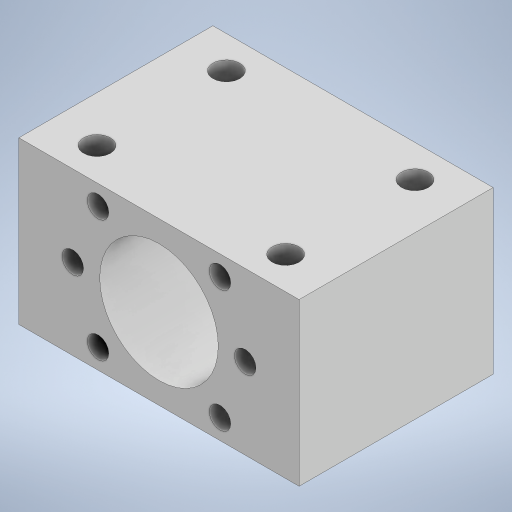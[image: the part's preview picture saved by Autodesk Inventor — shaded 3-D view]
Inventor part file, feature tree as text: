
AUTODESK INVENTOR PART (.ipt)
format: ipt  version: 2023 (Build 270158000, 158)  size: 224,768 bytes
history: native  units: mm
features: extrude x2, sketch x2
ambient origin geometry x8: Origin, YZ Plane, XZ Plane, XY Plane, X Axis, Y Axis, Z Axis, Center Point
bodies: Solid1 (feature_tree)
feature tree (4):
  extrude  "Extrusion1"  Depth=52.0mm
  extrude  "Extrusion3"  Depth=10.0mm
  sketch  "Sketch1"  dims[d0=22.0mm d2=52.0mm]
  sketch  "Sketch3"  dims[d3=32.0mm d4=4.0mm d5=45.0deg d6=15.0mm d9=36.0mm d10=0.0mm d16=30.0mm d17=5.0mm d18=35.0mm d19=24.0mm d20=10.0mm d21=0.0mm]
